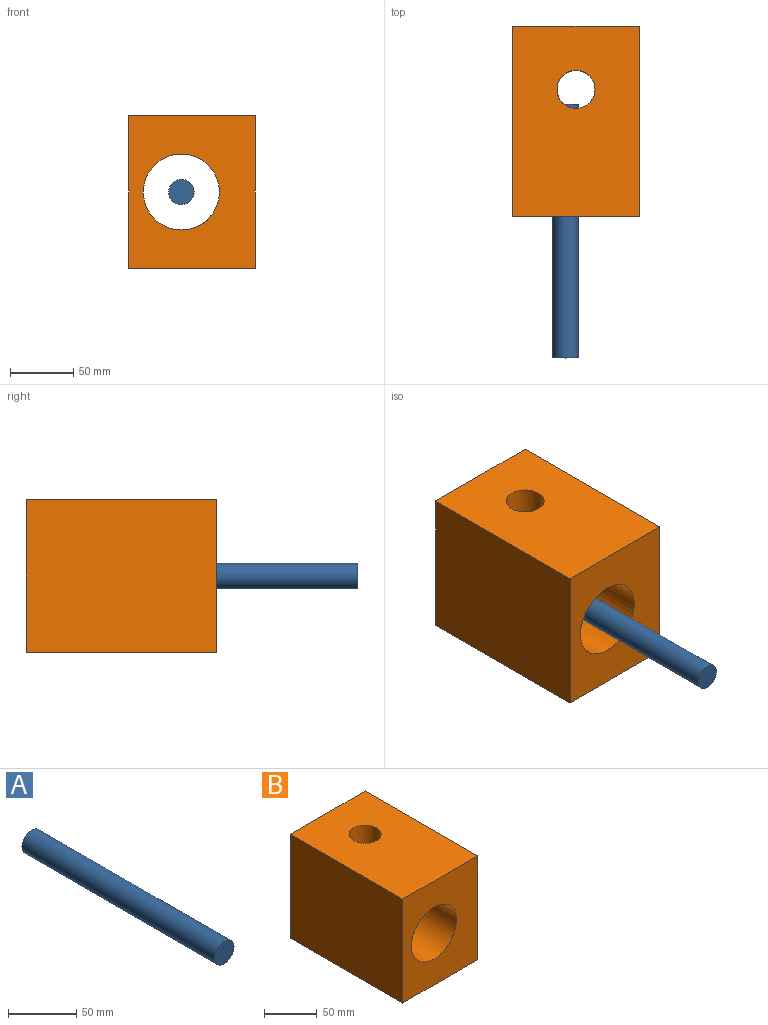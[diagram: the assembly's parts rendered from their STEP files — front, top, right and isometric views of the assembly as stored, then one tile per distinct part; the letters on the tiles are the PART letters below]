
ASSEMBLY  parts=2 mates=1
PART A: 3 faces, bbox 20x200x20 mm
  f0: cylinder r=10mm len=200mm, axis (0,1,0), area 12566.4mm2, adj f1,f2
  f1: plane 20x20mm, normal (0,-1,0), area 314.2mm2, adj f0
  f2: plane 20x20mm, normal (0,1,0), area 314.2mm2, adj f0
PART B: 9 faces, bbox 100x150x120 mm
  f0: plane 150x120mm, normal (1,0,0), area 18000mm2, adj f1,f3,f4,f5
  f1: plane 120x100mm, normal (0,1,0), area 9172.6mm2, adj f0,f2,f4,f5,f6
  f2: plane 150x120mm, normal (-1,0,0), area 18000mm2, adj f1,f3,f4,f5
  f3: plane 120x100mm, normal (0,-1,0), area 9172.6mm2, adj f0,f2,f4,f5,f6
  f4: plane 150x100mm, normal (0,0,1), area 14293.1mm2, adj f0,f1,f2,f3,f7
  f5: plane 150x100mm, normal (0,0,-1), area 14293.1mm2, adj f0,f1,f2,f3,f8
  f6: cylinder r=30mm len=150mm, axis (0,-1,0), area 26729.4mm2, adj f1,f3,f7,f8
  f7: cylinder r=15mm len=41.17mm, axis (0,0,1), area 3156.9mm2, adj f4,f6
  f8: cylinder r=15mm len=41.17mm, axis (0,0,1), area 3156.9mm2, adj f5,f6
PLACE A rot(axis=(0,-1,0),161.6deg) t=(74.95,13.26,29.1)mm
PLACE B t=(83.31,0,29.1)mm fixed
MATE cylindrical A.f0 <-> B.f6  axis (0,1,0) through (74.95,-86.74,29.1)mm
